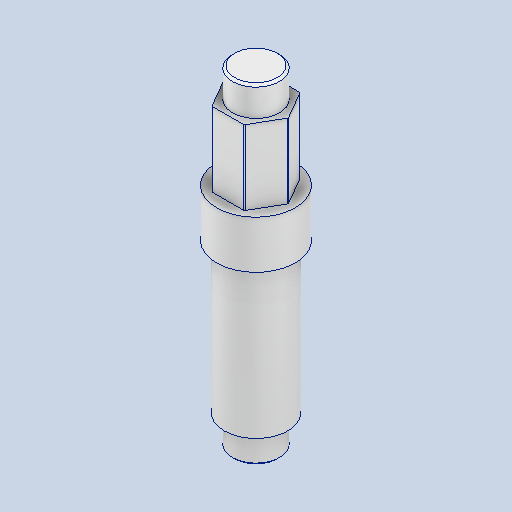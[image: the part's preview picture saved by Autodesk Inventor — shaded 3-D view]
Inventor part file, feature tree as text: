
AUTODESK INVENTOR PART (.ipt)
format: ipt  version: 2024 (Build 280153000, 153)  size: 116,224 bytes
history: native  units: in
note: dims shown in document units (in); Inventor stores cm internally (conversion verified against a paired STEP export)
features: chamfer x1
ambient origin geometry x8: Origin, YZ Plane, XZ Plane, XY Plane, X Axis, Y Axis, Z Axis, Center Point
bodies: Solid1 (feature_tree)
feature tree (1):
  chamfer  "Chamfer1"  [1 undecoded]
note: 1 required parameter value undecoded (feature->parameter linkage not recoverable at this tier; creation-order binding heuristic only, values carry confidence <= 0.55)
